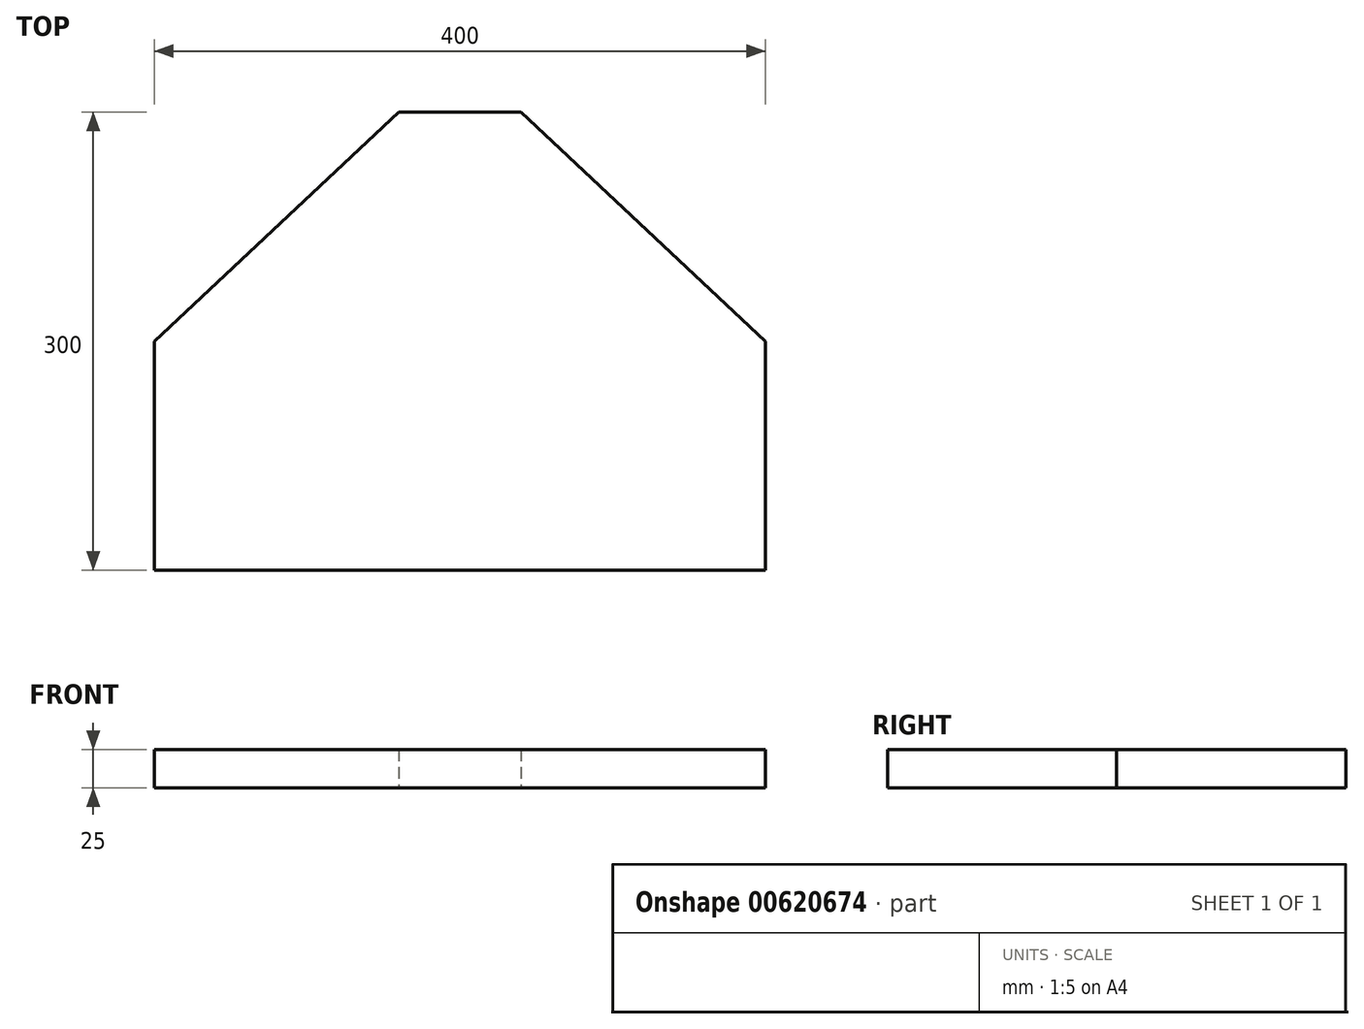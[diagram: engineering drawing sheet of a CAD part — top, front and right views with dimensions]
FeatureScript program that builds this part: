
annotation { "Feature Type Name" : "Feature", "Feature Type Description" : "" }
export const myFeature = defineFeature(function(context is Context, id is Id, definition is map)
    precondition{}
    {
        {
            var Q0;
            Q0=qCreatedBy(makeId("Top.planeOp"),FACE);
            var sketch = newSketch(context, id + "F0", { "sketchPlane" : qUnion([Q0])});
            skLineSegment(sketch, "E0.bottom", {"start": v(0, 0) * mm, "end": v(400, 0) * mm});
            skLineSegment(sketch, "E0.top", {"start": v(160, 300) * mm, "end": v(200, 300) * mm});
            skLineSegment(sketch, "E0.left", {"start": v(0, 0) * mm, "end": v(0, 150) * mm});
            skLineSegment(sketch, "E1", {"start": v(200, 300) * mm, "end": v(200, 0) * mm, "construction": true});
            skLineSegment(sketch, "E2", {"start": v(160, 300) * mm, "end": v(0, 150) * mm});
            skPoint(sketch, "E3.orphan", {"position": v(0, 300) * mm});
            skPoint(sketch, "E0.right.end.orphan", {"position": v(400, 300) * mm});
            skLineSegment(sketch, "E4.MirrorCS", {"start": v(240, 300) * mm, "end": v(200, 300) * mm});
            skLineSegment(sketch, "E5.MirrorCS", {"start": v(240, 300) * mm, "end": v(400, 150) * mm});
            skLineSegment(sketch, "E6.MirrorCS", {"start": v(400, 0) * mm, "end": v(400, 150) * mm});
            skSolve(sketch);
        }
        {
            var Q0;
            Q0 = qSketchRegion(id + "F0", true);
            extrude(context, id + "F1", {"entities" : qUnion([Q0]), "depth" : 25 * mm, "offsetDistance" : 25 * mm});
        }
    });
